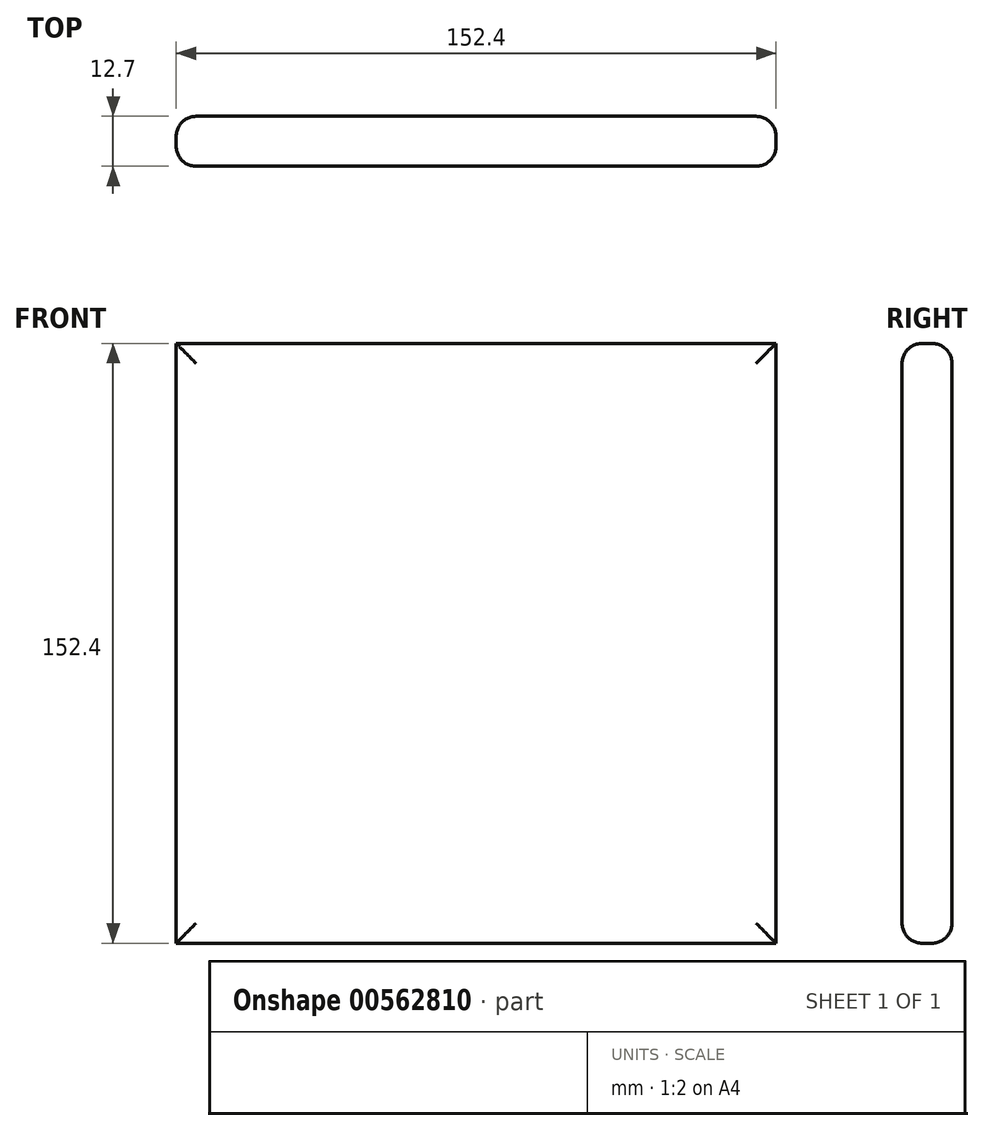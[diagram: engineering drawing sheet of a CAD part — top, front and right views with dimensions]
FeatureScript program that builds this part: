
annotation { "Feature Type Name" : "Feature", "Feature Type Description" : "" }
export const myFeature = defineFeature(function(context is Context, id is Id, definition is map)
    precondition{}
    {
        {
            var Q0;
            Q0=qCreatedBy(makeId("Front.planeOp"),FACE);
            var sketch = newSketch(context, id + "F0", { "sketchPlane" : qUnion([Q0])});
            skLineSegment(sketch, "E0.bottom", {"start": v(76.2, -76.2) * mm, "end": v(-76.2, -76.2) * mm});
            skLineSegment(sketch, "E0.top", {"start": v(76.2, 76.2) * mm, "end": v(-76.2, 76.2) * mm});
            skLineSegment(sketch, "E0.left", {"start": v(76.2, -76.2) * mm, "end": v(76.2, 76.2) * mm});
            skLineSegment(sketch, "E0.right", {"start": v(-76.2, -76.2) * mm, "end": v(-76.2, 76.2) * mm});
            skPoint(sketch, "E0.middle", {"position": v(0, 0) * mm});
            skPoint(sketch, "E1", {"position": v(50.8, 0) * mm});
            skPoint(sketch, "E2", {"position": v(-50.8, 0) * mm});
            skPoint(sketch, "E3", {"position": v(0, -50.8) * mm});
            skPoint(sketch, "E3.positionSnap0", {"position": v(0, -76.2) * mm});
            skPoint(sketch, "E4", {"position": v(0, 50.8) * mm});
            skSolve(sketch);
        }
        {
            var Q0;
            Q0 = qSketchRegion(id + "F0", true);
            extrude(context, id + "F1", {"entities" : qUnion([Q0]), "depth" : 12.7 * mm, "offsetDistance" : 25.4 * mm});
        }
        {
            var Q0;
            Q0=makeQuery(id+"F1.opExtrude","CAP_EDGE",EDGE,{"disambiguationData":[OSD([sQuery(id+"F0.wireOp",EDGE,"E0.left")])],"isStart":false});
            var Q1;
            Q1=makeQuery(id+"F1.opExtrude","CAP_EDGE",EDGE,{"disambiguationData":[OSD([sQuery(id+"F0.wireOp",EDGE,"E0.top")])],"isStart":false});
            var Q2;
            Q2=makeQuery(id+"F1.opExtrude","CAP_EDGE",EDGE,{"disambiguationData":[OSD([sQuery(id+"F0.wireOp",EDGE,"E0.right")])],"isStart":true});
            var Q3;
            Q3=makeQuery(id+"F1.opExtrude","CAP_EDGE",EDGE,{"disambiguationData":[OSD([sQuery(id+"F0.wireOp",EDGE,"E0.bottom")])],"isStart":false});
            var Q4;
            Q4=makeQuery(id+"F1.opExtrude","CAP_EDGE",EDGE,{"disambiguationData":[OSD([sQuery(id+"F0.wireOp",EDGE,"E0.right")])],"isStart":false});
            var Q5;
            Q5=makeQuery(id+"F1.opExtrude","CAP_EDGE",EDGE,{"disambiguationData":[OSD([sQuery(id+"F0.wireOp",EDGE,"E0.bottom")])],"isStart":true});
            var Q6;
            Q6=makeQuery(id+"F1.opExtrude","CAP_EDGE",EDGE,{"disambiguationData":[OSD([sQuery(id+"F0.wireOp",EDGE,"E0.left")])],"isStart":true});
            var Q7;
            Q7=makeQuery(id+"F1.opExtrude","CAP_EDGE",EDGE,{"disambiguationData":[OSD([sQuery(id+"F0.wireOp",EDGE,"E0.top")])],"isStart":true});
            fillet(context, id + "F2", {"entities" : qUnion([Q0, Q1, Q2, Q3, Q4, Q5, Q6, Q7]), "radius" : 5.08 * mm, "tangentPropagation" : true, "allowEdgeOverflow" : false});
        }
    });
